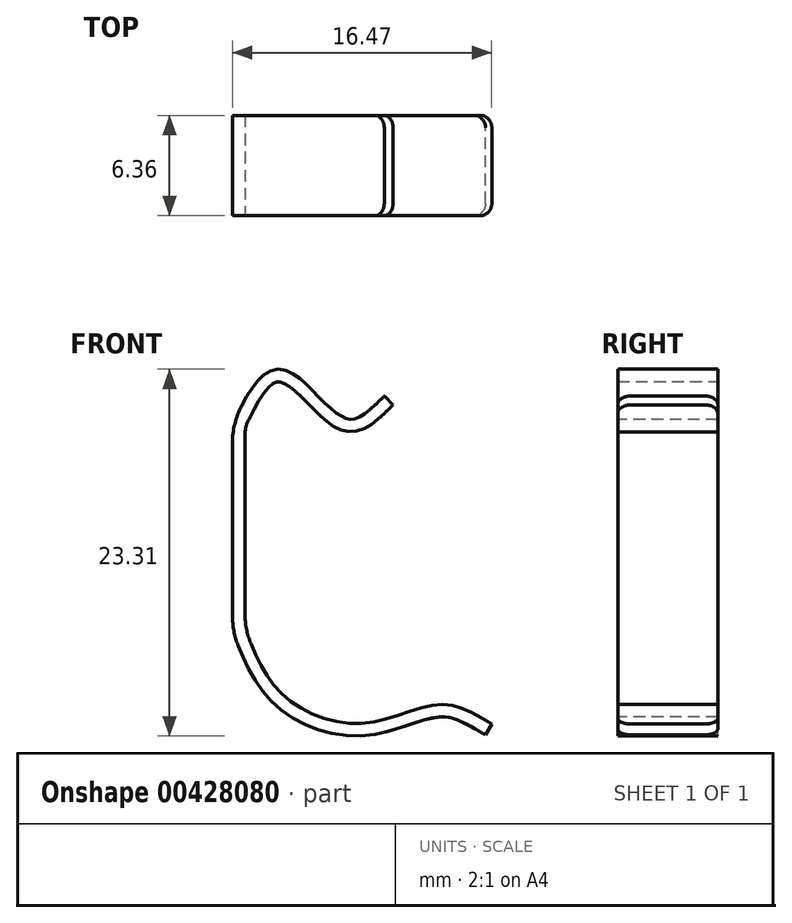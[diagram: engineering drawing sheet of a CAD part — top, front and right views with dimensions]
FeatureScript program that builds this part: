
annotation { "Feature Type Name" : "Feature", "Feature Type Description" : "" }
export const myFeature = defineFeature(function(context is Context, id is Id, definition is map)
    precondition{}
    {
        {
            var Q0;
            Q0=qCreatedBy(makeId("Front.planeOp"),FACE);
            var sketch = newSketch(context, id + "F0", { "sketchPlane" : qUnion([Q0])});
            skLineSegment(sketch, "E0", {"start": v(0, 2.92) * mm, "end": v(15.88, 2.92) * mm});
            skLineSegment(sketch, "E1", {"start": v(0, 25.4) * mm, "end": v(9.53, 25.4) * mm});
            skLineSegment(sketch, "E2", {"start": v(9.53, 25.4) * mm, "end": v(9.53, 22.23) * mm});
            skLineSegment(sketch, "E3", {"start": v(9.53, 22.23) * mm, "end": v(0, 22.23) * mm});
            skLineSegment(sketch, "E4", {"start": v(0, 25.4) * mm, "end": v(4.76, 25.4) * mm});
            skLineSegment(sketch, "E5", {"start": v(0, 22.23) * mm, "end": v(4.76, 22.23) * mm});
            skLineSegment(sketch, "E6", {"start": v(0, 22.23) * mm, "end": v(0, 25.4) * mm});
            skLineSegment(sketch, "E7", {"start": v(0, 23.81) * mm, "end": v(9.53, 23.81) * mm});
            skLineSegment(sketch, "E8", {"start": v(4.76, 25.4) * mm, "end": v(4.76, 22.23) * mm});
            skLineSegment(sketch, "E9", {"start": v(4.76, 22.23) * mm, "end": v(9.53, 22.23) * mm});
            skLineSegment(sketch, "E10", {"start": v(0, 2.92) * mm, "end": v(0, 9.27) * mm});
            skLineSegment(sketch, "E11", {"start": v(0, 2.92) * mm, "end": v(7.94, 2.92) * mm});
            skLineSegment(sketch, "E12", {"start": v(0, 2.92) * mm, "end": v(12.7, 2.92) * mm});
            skLineSegment(sketch, "E13", {"start": v(12.7, 2.92) * mm, "end": v(12.7, 4.11) * mm});
            skLineSegment(sketch, "E14", {"start": v(1.27, 2.92) * mm, "end": v(2.54, 2.92) * mm});
            skLineSegment(sketch, "E15", {"start": v(2.54, 2.92) * mm, "end": v(2.54, 4.83) * mm});
            skPoint(sketch, "E16.newPointB", {"position": v(0, 0) * mm});
            skPoint(sketch, "E17.newPointB", {"position": v(0, 25.4) * mm});
            skFitSpline(sketch, "E18", {"points": [v(0, 22.23) * mm, v(2.38, 25.4) * mm, v(4.76, 23.81) * mm, v(7.14, 22.23) * mm, v(9.53, 23.81) * mm], "startDerivative": vector(8.02, 16.16) * mm, "endDerivative": vector(9.97, 9.9) * mm});
            skFitSpline(sketch, "E19", {"points": [v(0, 9.27) * mm, v(2.54, 4.83) * mm, v(7.94, 2.92) * mm, v(12.7, 4.11) * mm, v(15.88, 2.92) * mm], "startDerivative": vector(6.89, -18.64) * mm, "endDerivative": vector(19.07, -10.97) * mm});
            skLineSegment(sketch, "E20", {"start": v(0, 9.27) * mm, "end": v(0, 14.29) * mm});
            skLineSegment(sketch, "E21", {"start": v(0, 14.29) * mm, "end": v(0, 22.23) * mm});
            skSolve(sketch);
        }
        {
            var Q0;
            Q0=qCreatedBy(makeId("Top.planeOp"),FACE);
            var Q1;
            Q1=sQuery(id+"F0.wireOp",VERTEX,"E20.end");
            cPlane(context, id + "F1", {"entities" : qUnion([Q0, Q1]), "cplaneType" : CPlaneType.PLANE_POINT, "offset" : 25.4 * mm, "width" : 152.4 * mm, "height" : 152.4 * mm});
        }
        {
            var Q0;
            Q0=qCreatedBy(id+"F1.planeOp",FACE);
            var sketch = newSketch(context, id + "F2", { "sketchPlane" : qUnion([Q0])});
            skPoint(sketch, "E22.0", {"position": v(0, 0) * mm});
            skLineSegment(sketch, "E23.bottom", {"start": v(-0.4, -3.17) * mm, "end": v(0.4, -3.17) * mm});
            skLineSegment(sketch, "E23.top", {"start": v(-0.4, 3.18) * mm, "end": v(0.4, 3.18) * mm});
            skLineSegment(sketch, "E23.left", {"start": v(-0.4, -3.17) * mm, "end": v(-0.4, 3.18) * mm});
            skLineSegment(sketch, "E23.right", {"start": v(0.4, -3.17) * mm, "end": v(0.4, 3.18) * mm});
            skSolve(sketch);
        }
        {
            var Q0;
            Q0=makeQuery(id+"F2.imprint","IMPRINT",FACE,{"disambiguationData":[TD([[makeQuery(id+"F2.imprint","IMPRINT",EDGE,{"derivedFrom":sQuery(id+"F2.wireOp",EDGE,"E23.bottom")}),1.0]])]});
            var Q1;
            Q1=sQuery(id+"F0.wireOp",EDGE,"E20");
            var Q2;
            Q2=sQuery(id+"F0.wireOp",EDGE,"E19");
            sweep(context, id + "F3", {"profiles" : qUnion([Q0]), "path" : qUnion([Q1, Q2])});
        }
        {
            var Q0;
            Q0=makeQuery(id+"F2.imprint","IMPRINT",FACE,{"disambiguationData":[TD([[makeQuery(id+"F2.imprint","IMPRINT",EDGE,{"derivedFrom":sQuery(id+"F2.wireOp",EDGE,"E23.bottom")}),1.0]])]});
            var Q1;
            Q1=sQuery(id+"F0.wireOp",EDGE,"E21");
            var Q2;
            Q2=sQuery(id+"F0.wireOp",EDGE,"E18");
            sweep(context, id + "F4", {"operationType" : NewBodyOperationType.ADD, "profiles" : qUnion([Q0]), "path" : qUnion([Q1, Q2])});
        }
        {
            var Q0;
            Q0=makeQuery(id+"F4.opSweep","MID_CAP_EDGE",EDGE,{"disambiguationData":[OSD([sQuery(id+"F0.wireOp",VERTEX,"E18.start"),sQuery(id+"F2.wireOp",EDGE,"E23.left")])],"capPos":1.0});
            var Q1;
            Q1=makeQuery(id+"F3.opSweep","MID_CAP_EDGE",EDGE,{"disambiguationData":[OSD([sQuery(id+"F0.wireOp",VERTEX,"E19.start"),sQuery(id+"F2.wireOp",EDGE,"E23.right")])],"capPos":1.0});
            var Q2;
            Q2=makeQuery(id+"F3.opSweep","MID_CAP_EDGE",EDGE,{"disambiguationData":[OSD([sQuery(id+"F0.wireOp",VERTEX,"E19.start"),sQuery(id+"F2.wireOp",EDGE,"E23.left")])],"capPos":1.0});
            fillet(context, id + "F5", {"entities" : qUnion([Q0, Q1, Q2]), "radius" : 5.08 * mm, "tangentPropagation" : true, "allowEdgeOverflow" : false});
        }
        {
            var Q0;
            Q0=makeQuery(id+"F4.opSweep","CAP_EDGE",EDGE,{"disambiguationData":[OSD([sQuery(id+"F0.wireOp",VERTEX,"E18.end"),sQuery(id+"F2.wireOp",EDGE,"E23.bottom")])],"isStart":false});
            var Q1;
            Q1=makeQuery(id+"F4.opSweep","CAP_EDGE",EDGE,{"disambiguationData":[OSD([sQuery(id+"F0.wireOp",VERTEX,"E18.end"),sQuery(id+"F2.wireOp",EDGE,"E23.top")])],"isStart":false});
            var Q2;
            Q2=makeQuery(id+"F3.opSweep","CAP_EDGE",EDGE,{"disambiguationData":[OSD([sQuery(id+"F0.wireOp",VERTEX,"E19.end"),sQuery(id+"F2.wireOp",EDGE,"E23.bottom")])],"isStart":false});
            var Q3;
            Q3=makeQuery(id+"F3.opSweep","CAP_EDGE",EDGE,{"disambiguationData":[OSD([sQuery(id+"F0.wireOp",VERTEX,"E19.end"),sQuery(id+"F2.wireOp",EDGE,"E23.top")])],"isStart":false});
            fillet(context, id + "F6", {"entities" : qUnion([Q0, Q1, Q2, Q3]), "radius" : 0.76 * mm, "allowEdgeOverflow" : false});
        }
        {
            var Q0;
            Q0=makeQuery(id+"F4.opSweep","MID_CAP_EDGE",EDGE,{"disambiguationData":[OSD([sQuery(id+"F0.wireOp",VERTEX,"E18.start"),sQuery(id+"F2.wireOp",EDGE,"E23.right")])],"capPos":1.0});
            fillet(context, id + "F7", {"entities" : qUnion([Q0]), "radius" : 2.3 * mm, "allowEdgeOverflow" : false});
        }
        {
            var Q0;
            {var subQ0=sQuery(id+"F0.wireOp",EDGE,"E1");Q0=makeQuery(id+"F0.imprint","IMPRINT",FACE,{"disambiguationData":[TD([[makeQuery(id+"F0.imprint","IMPRINT",EDGE,{"derivedFrom":subQ0}),-1.0]])]});}
            var sketch = newSketch(context, id + "F8", { "sketchPlane" : qUnion([Q0])});
            skFitSpline(sketch, "E24.0", {"points": [v(0.36, 22.05) * mm, v(0.73, 22.8) * mm, v(1.1, 23.56) * mm, v(1.66, 24.39) * mm, v(1.84, 24.61) * mm, v(2.18, 24.92) * mm, v(2.33, 24.99) * mm, v(2.64, 25.04) * mm, v(2.94, 24.92) * mm, v(3.67, 24.36) * mm, v(4.07, 23.95) * mm, v(4.88, 23.12) * mm, v(5.3, 22.7) * mm, v(6.15, 22.07) * mm, v(6.62, 21.82) * mm, v(7.67, 21.83) * mm, v(8.14, 22.09) * mm, v(9, 22.73) * mm, v(9.4, 23.14) * mm, v(9.8, 23.53) * mm]});
            skFitSpline(sketch, "E25.0", {"points": [v(9.26, 23) * mm, v(9.33, 23.07) * mm, v(9.47, 23.2) * mm, v(9.72, 23.44) * mm, v(9.8, 23.53) * mm, v(9.8, 23.53) * mm]});
            skSolve(sketch);
        }
        {
            var Q0;
            Q0=makeQuery(id+"F6.opFillet","BLEND_EDGE",EDGE,{"blendedFrom":[makeQuery(id+"F4.opSweep","CAP_EDGE",EDGE,{"disambiguationData":[OSD([sQuery(id+"F0.wireOp",VERTEX,"E18.end"),sQuery(id+"F2.wireOp",EDGE,"E23.bottom")])],"isStart":false}),makeQuery(id+"F4.opSweep","SWEPT_FACE",FACE,{"disambiguationData":[OSD([sQuery(id+"F0.wireOp",EDGE,"E18"),sQuery(id+"F2.wireOp",EDGE,"E23.right")])]})],"blendedInto":[makeQuery(id+"F4.opSweep","SWEPT_FACE",FACE,{"disambiguationData":[OSD([sQuery(id+"F0.wireOp",EDGE,"E18"),sQuery(id+"F2.wireOp",EDGE,"E23.right")])]})]});
            cPoint(context, id + "F9", {"entities" : qUnion([Q0]), "parameter" : 0.5});
        }
        {
            var Q0;
            Q0=sQuery(id+"F8.wireOp",VERTEX,"E25.0.start");
            var Q1;
            Q1=sQuery(id+"F8.wireOp",VERTEX,"E25.0.end");
            var Q2;
            Q2 = qCreatedBy(id + "F9" ,VERTEX);
            cPlane(context, id + "F10", {"entities" : qUnion([Q0, Q1, Q2]), "cplaneType" : CPlaneType.THREE_POINT, "offset" : 25.4 * mm, "width" : 152.4 * mm, "height" : 152.4 * mm});
        }
        {
            var Q0;
            Q0=qCreatedBy(id+"F10.planeOp",FACE);
            var sketch = newSketch(context, id + "F11", { "sketchPlane" : qUnion([Q0])});
            skPoint(sketch, "E26.0", {"position": v(22.7, 0.02) * mm});
            skPoint(sketch, "E27.0", {"position": v(23.45, 0.02) * mm});
            skFitSpline(sketch, "E28.0", {"points": [v(22.7, 0.03) * mm, v(22.8, 0.03) * mm, v(22.99, 0.03) * mm, v(23.33, 0.03) * mm, v(23.45, 0.03) * mm, v(23.45, 0.03) * mm]});
            skSolve(sketch);
        }
        {
            var Q0;
            Q0=makeQuery(id+"F4.opSweep","CAP_EDGE",EDGE,{"disambiguationData":[OSD([sQuery(id+"F0.wireOp",VERTEX,"E18.end"),sQuery(id+"F2.wireOp",EDGE,"E23.left")])],"isStart":false});
            cPoint(context, id + "F12", {"entities" : qUnion([Q0]), "parameter" : 0.5});
        }
        {
            var Q0;
            Q0=sQuery(id+"F11.wireOp",VERTEX,"E26.0");
            var Q1;
            Q1=sQuery(id+"F11.wireOp",VERTEX,"E27.0");
            var Q2;
            Q2 = qCreatedBy(id + "F12" ,VERTEX);
            cPlane(context, id + "F13", {"entities" : qUnion([Q0, Q1, Q2]), "cplaneType" : CPlaneType.THREE_POINT, "offset" : 25.4 * mm, "width" : 152.4 * mm, "height" : 152.4 * mm});
        }
        {
            var Q0;
            Q0=qCreatedBy(id+"F13.planeOp",FACE);
            var sketch = newSketch(context, id + "F14", { "sketchPlane" : qUnion([Q0])});
            skPoint(sketch, "E29.0", {"position": v(-9.26, 23) * mm});
            skLineSegment(sketch, "E30", {"start": v(-9.26, 23) * mm, "end": v(-9.28, 22.98) * mm});
            skSolve(sketch);
        }
    });
